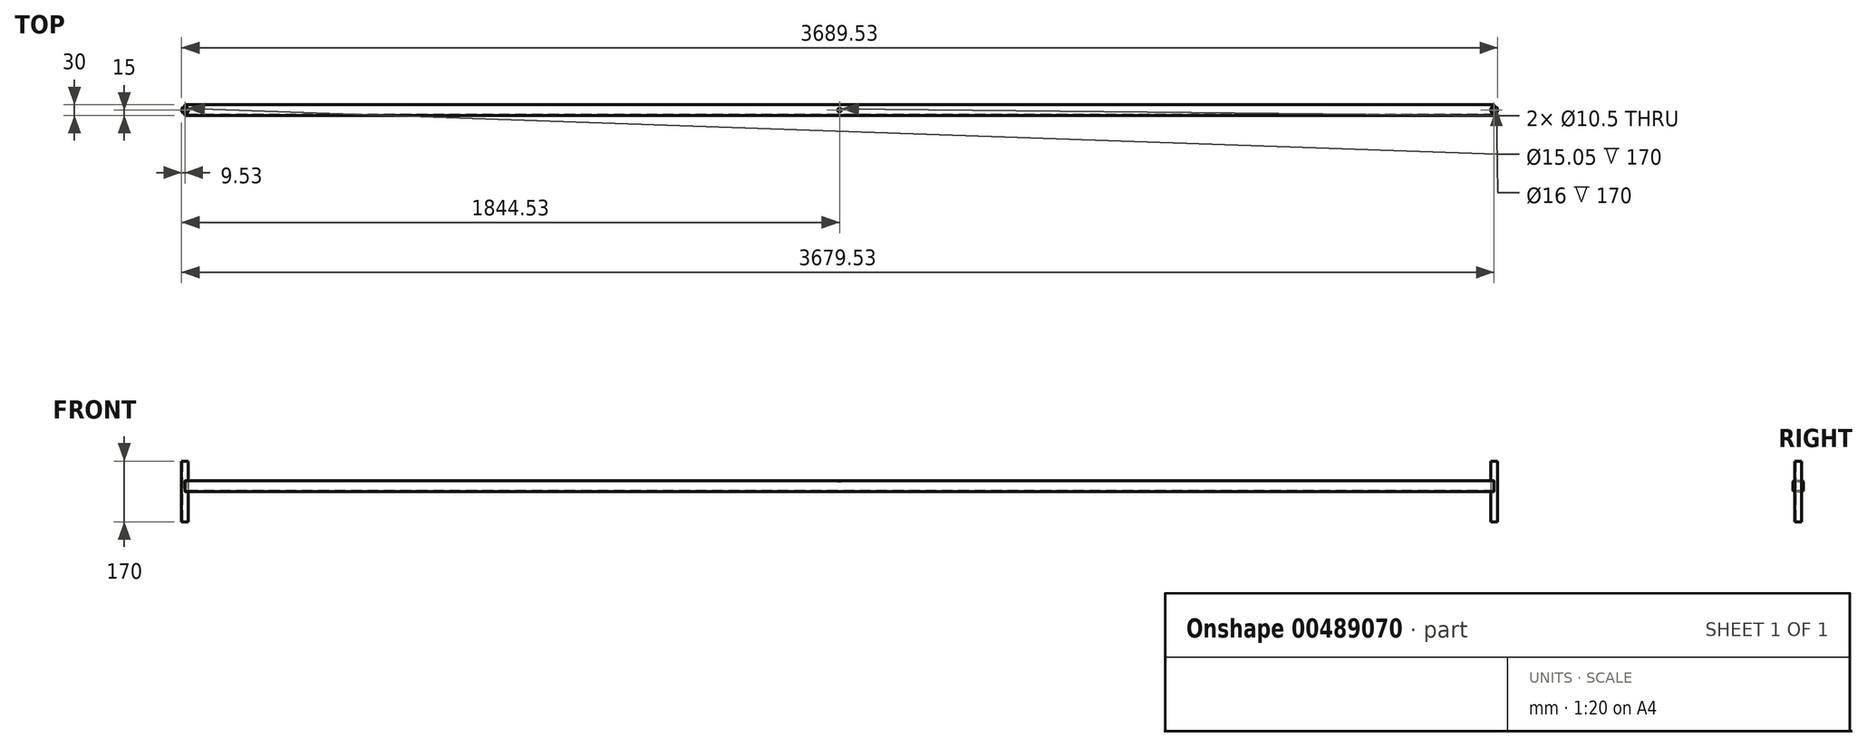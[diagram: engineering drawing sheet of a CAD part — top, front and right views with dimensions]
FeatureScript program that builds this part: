
annotation { "Feature Type Name" : "Feature", "Feature Type Description" : "" }
export const myFeature = defineFeature(function(context is Context, id is Id, definition is map)
    precondition{}
    {
        {
            var Q0;
            Q0=qCreatedBy(makeId("Right.planeOp"),FACE);
            var sketch = newSketch(context, id + "F0", { "sketchPlane" : qUnion([Q0])});
            skLineSegment(sketch, "E0.bottom", {"start": v(10, -15) * mm, "end": v(-10, -15) * mm});
            skLineSegment(sketch, "E0.top", {"start": v(10, 15) * mm, "end": v(-10, 15) * mm});
            skLineSegment(sketch, "E0.left", {"start": v(15, -10) * mm, "end": v(15, 10) * mm});
            skLineSegment(sketch, "E0.right", {"start": v(-15, -10) * mm, "end": v(-15, 10) * mm});
            skPoint(sketch, "E0.middle", {"position": v(0, 0) * mm});
            skPoint(sketch, "E1.visualSharp", {"position": v(-15, 15) * mm});
            skArc(sketch, "E1.filletArc", {"start": v(-10, 15) * mm, "mid": v(-13.54, 13.54) * mm, "end": v(-15, 10) * mm});
            skPoint(sketch, "E2.visualSharp", {"position": v(15, 15) * mm});
            skArc(sketch, "E2.filletArc", {"start": v(15, 10) * mm, "mid": v(13.54, 13.54) * mm, "end": v(10, 15) * mm});
            skPoint(sketch, "E3.visualSharp", {"position": v(15, -15) * mm});
            skArc(sketch, "E3.filletArc", {"start": v(10, -15) * mm, "mid": v(13.54, -13.54) * mm, "end": v(15, -10) * mm});
            skPoint(sketch, "E4.visualSharp", {"position": v(-15, -15) * mm});
            skArc(sketch, "E4.filletArc", {"start": v(-15, -10) * mm, "mid": v(-13.54, -13.54) * mm, "end": v(-10, -15) * mm});
            skArc(sketch, "E5.0", {"start": v(12.5, 10) * mm, "mid": v(11.77, 11.77) * mm, "end": v(10, 12.5) * mm});
            skLineSegment(sketch, "E5.1", {"start": v(12.5, -10) * mm, "end": v(12.5, 10) * mm});
            skLineSegment(sketch, "E5.2", {"start": v(10, 12.5) * mm, "end": v(-10, 12.5) * mm});
            skArc(sketch, "E5.3", {"start": v(10, -12.5) * mm, "mid": v(11.77, -11.77) * mm, "end": v(12.5, -10) * mm});
            skArc(sketch, "E5.4", {"start": v(-10, 12.5) * mm, "mid": v(-11.77, 11.77) * mm, "end": v(-12.5, 10) * mm});
            skLineSegment(sketch, "E5.5", {"start": v(-12.5, -10) * mm, "end": v(-12.5, 10) * mm});
            skArc(sketch, "E5.6", {"start": v(-12.5, -10) * mm, "mid": v(-11.77, -11.77) * mm, "end": v(-10, -12.5) * mm});
            skLineSegment(sketch, "E5.7", {"start": v(10, -12.5) * mm, "end": v(-10, -12.5) * mm});
            skSolve(sketch);
        }
        {
            var Q0;
            Q0 = qSketchRegion(id + "F0", true);
            extrude(context, id + "F1", {"entities" : qUnion([Q0]), "depth" : 3670 * mm, "symmetric" : true});
        }
        {
            var Q0;
            Q0=makeQuery(id+"F1.opExtrude","SWEPT_FACE",FACE,{"disambiguationData":[OSD([sQuery(id+"F0.wireOp",EDGE,"E0.top")])]});
            var sketch = newSketch(context, id + "F2", { "sketchPlane" : qUnion([Q0])});
            skCircle(sketch, "E6", {"center": v(-1835, 0) * mm, "radius": 10 * mm});
            skCircle(sketch, "E7", {"center": v(1835, 0) * mm, "radius": 10 * mm});
            skSolve(sketch);
        }
        {
            var Q0;
            Q0 = qSketchRegion(id + "F2", true);
            extrude(context, id + "F3", {"entities" : qUnion([Q0]), "operationType" : NewBodyOperationType.REMOVE, "endBound" : BoundingType.THROUGH_ALL, "oppositeDirection" : true, "depth" : 25 * mm});
        }
        {
            var Q0;
            Q0=qCreatedBy(makeId("Top.planeOp"),FACE);
            var sketch = newSketch(context, id + "F4", { "sketchPlane" : qUnion([Q0])});
            skCircle(sketch, "E8", {"center": v(-1835, 0) * mm, "radius": 9.53 * mm});
            skCircle(sketch, "E9", {"center": v(1835, 0) * mm, "radius": 10 * mm});
            skCircle(sketch, "E10", {"center": v(-1835, 0) * mm, "radius": 7.53 * mm});
            skCircle(sketch, "E11", {"center": v(1835, 0) * mm, "radius": 8 * mm});
            skSolve(sketch);
        }
        {
            var Q0;
            Q0 = qSketchRegion(id + "F4", true);
            extrude(context, id + "F5", {"entities" : qUnion([Q0]), "operationType" : NewBodyOperationType.ADD, "depth" : 70 * mm, "hasSecondDirection" : true, "secondDirectionOppositeDirection" : true, "secondDirectionDepth" : 100 * mm});
        }
        {
            var Q0;
            Q0=makeQuery(id+"F1.opExtrude","SWEPT_FACE",FACE,{"disambiguationData":[OSD([sQuery(id+"F0.wireOp",EDGE,"E0.top")])]});
            var sketch = newSketch(context, id + "F6", { "sketchPlane" : qUnion([Q0])});
            skCircle(sketch, "E12", {"center": v(0, 0) * mm, "radius": 5.25 * mm});
            skSolve(sketch);
        }
        {
            var Q0;
            Q0 = qSketchRegion(id + "F6", true);
            extrude(context, id + "F7", {"entities" : qUnion([Q0]), "operationType" : NewBodyOperationType.REMOVE, "endBound" : BoundingType.THROUGH_ALL, "oppositeDirection" : true, "depth" : 25 * mm});
        }
    });
